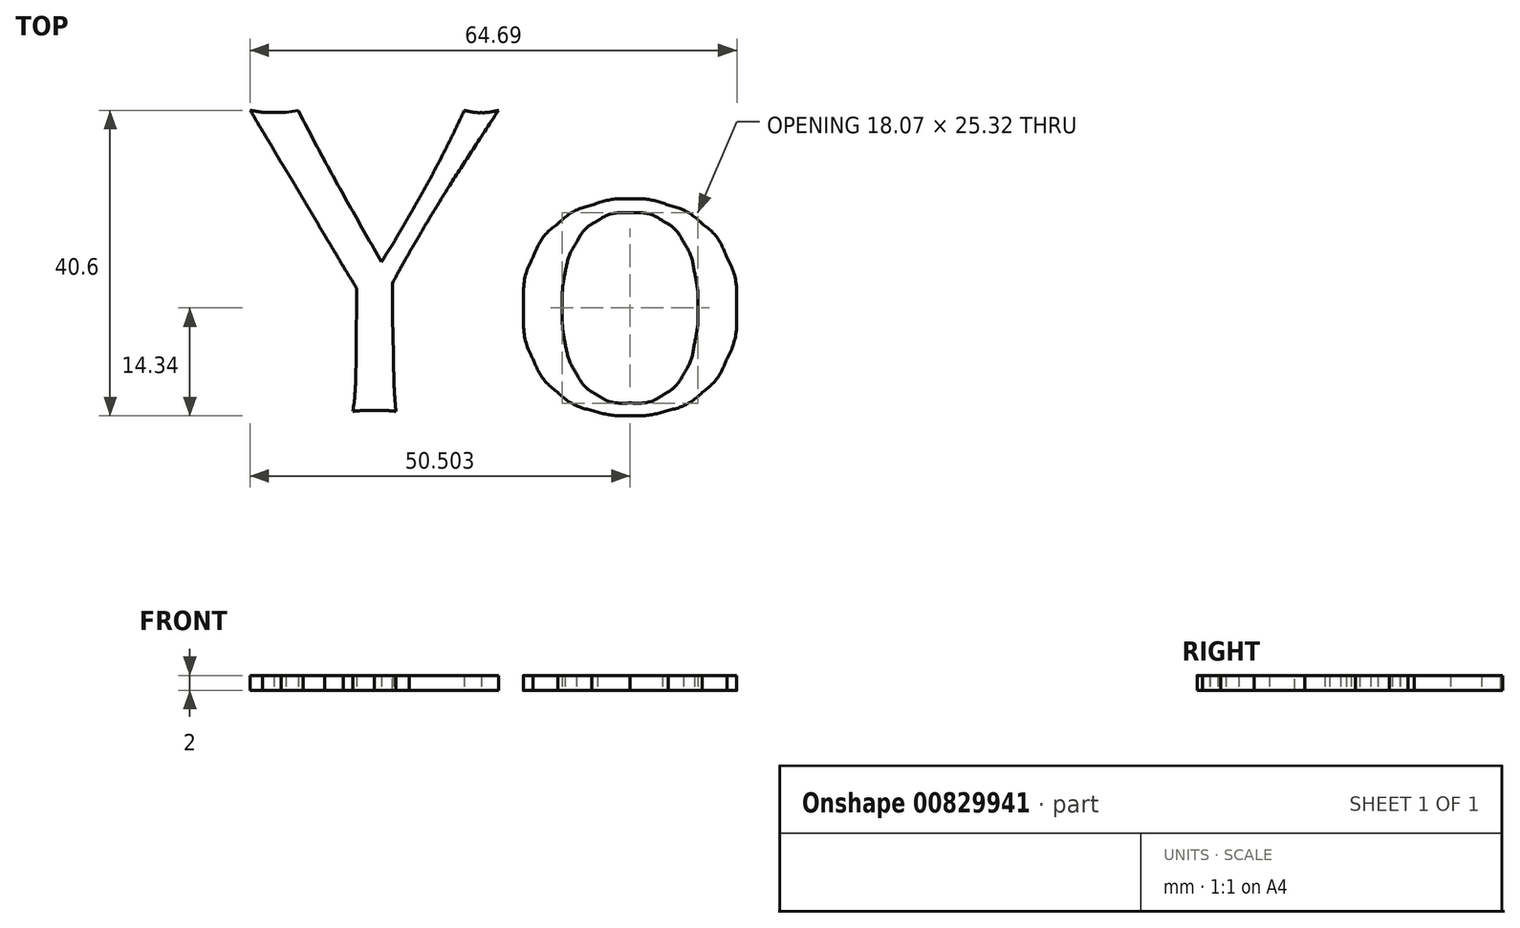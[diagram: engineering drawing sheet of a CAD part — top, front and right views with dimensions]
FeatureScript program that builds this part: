
annotation { "Feature Type Name" : "Feature", "Feature Type Description" : "" }
export const myFeature = defineFeature(function(context is Context, id is Id, definition is map)
    precondition{}
    {
        {
            var Q0;
            Q0=qCreatedBy(makeId("Top.planeOp"),FACE);
            var sketch = newSketch(context, id + "F0", { "sketchPlane" : qUnion([Q0])});
            skLineSegment(sketch, "E0", {"start": v(10.7, 31.08) * mm, "end": v(10.7, 30.96) * mm});
            skLineSegment(sketch, "E1", {"start": v(10.7, 30.96) * mm, "end": v(10.7, 31.08) * mm});
            skLineSegment(sketch, "E2", {"start": v(10.23, 21.47) * mm, "end": v(10.23, 21.36) * mm});
            skLineSegment(sketch, "E3", {"start": v(10.23, 21.36) * mm, "end": v(10.23, 21.47) * mm});
            skLineSegment(sketch, "E4", {"start": v(23.04, 46.92) * mm, "end": v(23.15, 47.03) * mm});
            skLineSegment(sketch, "E5", {"start": v(23.15, 47.03) * mm, "end": v(23.04, 46.92) * mm});
            skLineSegment(sketch, "E6", {"start": v(50.58, 35.45) * mm, "end": v(50.34, 26.71) * mm});
            skLineSegment(sketch, "E7", {"start": v(50.34, 26.71) * mm, "end": v(50.58, 35.45) * mm});
            skLineSegment(sketch, "E8", {"start": v(36.2, 45.81) * mm, "end": v(36.2, 42.78) * mm});
            skLineSegment(sketch, "E9", {"start": v(36.2, 42.78) * mm, "end": v(36.84, 42.78) * mm});
            skLineSegment(sketch, "E10", {"start": v(36.84, 42.78) * mm, "end": v(36.2, 45.81) * mm});
            skLineSegment(sketch, "E11", {"start": v(58.26, 21.65) * mm, "end": v(58.26, 22.93) * mm});
            skLineSegment(sketch, "E12", {"start": v(58.26, 22.93) * mm, "end": v(58.26, 21.65) * mm});
            skLineSegment(sketch, "E13", {"start": v(-22.09, -30.8) * mm, "end": v(-22.79, -30.8) * mm});
            skLineSegment(sketch, "E14", {"start": v(-22.79, -30.8) * mm, "end": v(-22.09, -30.8) * mm});
            skLineSegment(sketch, "E15", {"start": v(-9.57, -13.74) * mm, "end": v(-8.87, -13.74) * mm});
            skLineSegment(sketch, "E16", {"start": v(-8.87, -13.74) * mm, "end": v(-9.57, -13.74) * mm});
            skLineSegment(sketch, "E17", {"start": v(5.02, -26.08) * mm, "end": v(5.02, -26.2) * mm});
            skLineSegment(sketch, "E18", {"start": v(5.02, -26.2) * mm, "end": v(5.02, -26.08) * mm});
            skLineSegment(sketch, "E19", {"start": v(4.56, -35.7) * mm, "end": v(4.56, -35.8) * mm});
            skLineSegment(sketch, "E20", {"start": v(4.56, -35.8) * mm, "end": v(4.56, -35.7) * mm});
            skLineSegment(sketch, "E21", {"start": v(17.37, -10.25) * mm, "end": v(17.48, -10.13) * mm});
            skLineSegment(sketch, "E22", {"start": v(17.48, -10.13) * mm, "end": v(17.37, -10.25) * mm});
            skFitSpline(sketch, "E23", {"points": [v(-50.5, 37.3) * mm, v(-50.5, 34.17) * mm, v(-50.52, 31.16) * mm, v(-50.56, 28.29) * mm]});
            skFitSpline(sketch, "E24", {"points": [v(-50.56, 28.29) * mm, v(-50.6, 25.41) * mm, v(-50.73, 22.97) * mm, v(-50.96, 20.95) * mm]});
            skFitSpline(sketch, "E25", {"points": [v(-50.96, 20.95) * mm, v(-50.07, 21.03) * mm, v(-49.12, 21.07) * mm, v(-48.11, 21.07) * mm]});
            skFitSpline(sketch, "E26", {"points": [v(-48.11, 21.07) * mm, v(-47.1, 21.07) * mm, v(-46.15, 21.03) * mm, v(-45.26, 20.95) * mm]});
            skFitSpline(sketch, "E27", {"points": [v(-45.26, 20.95) * mm, v(-45.34, 21.76) * mm, v(-45.41, 22.83) * mm, v(-45.5, 24.15) * mm]});
            skFitSpline(sketch, "E28", {"points": [v(-45.5, 24.15) * mm, v(-45.53, 25.5) * mm, v(-45.57, 26.97) * mm, v(-45.6, 28.52) * mm]});
            skFitSpline(sketch, "E29", {"points": [v(-45.6, 28.52) * mm, v(-45.65, 30.1) * mm, v(-45.69, 31.72) * mm, v(-45.72, 33.35) * mm]});
            skFitSpline(sketch, "E30", {"points": [v(-45.72, 33.35) * mm, v(-45.72, 34.98) * mm, v(-45.72, 36.51) * mm, v(-45.72, 37.95) * mm]});
            skFitSpline(sketch, "E31", {"points": [v(-45.72, 37.95) * mm, v(-45.1, 39.15) * mm, v(-44.37, 40.5) * mm, v(-43.51, 41.97) * mm]});
            skFitSpline(sketch, "E32", {"points": [v(-43.51, 41.97) * mm, v(-42.66, 43.48) * mm, v(-41.67, 45.17) * mm, v(-40.54, 47.03) * mm]});
            skFitSpline(sketch, "E33", {"points": [v(-40.54, 47.03) * mm, v(-39.42, 48.9) * mm, v(-38.12, 50.97) * mm, v(-36.64, 53.26) * mm]});
            skFitSpline(sketch, "E34", {"points": [v(-36.64, 53.26) * mm, v(-35.17, 55.55) * mm, v(-33.5, 58.12) * mm, v(-31.63, 60.95) * mm]});
            skFitSpline(sketch, "E35", {"points": [v(-31.63, 60.95) * mm, v(-32.6, 60.75) * mm, v(-33.36, 60.66) * mm, v(-33.9, 60.66) * mm]});
            skFitSpline(sketch, "E36", {"points": [v(-33.9, 60.66) * mm, v(-34.45, 60.66) * mm, v(-35.2, 60.75) * mm, v(-36.18, 60.95) * mm]});
            skFitSpline(sketch, "E37", {"points": [v(-36.18, 60.95) * mm, v(-36.95, 59.28) * mm, v(-37.79, 57.55) * mm, v(-38.68, 55.77) * mm]});
            skFitSpline(sketch, "E38", {"points": [v(-38.68, 55.77) * mm, v(-39.57, 54.02) * mm, v(-40.5, 52.27) * mm, v(-41.47, 50.53) * mm]});
            skFitSpline(sketch, "E39", {"points": [v(-41.47, 50.53) * mm, v(-42.44, 48.78) * mm, v(-43.41, 47.07) * mm, v(-44.39, 45.4) * mm]});
            skFitSpline(sketch, "E40", {"points": [v(-44.39, 45.4) * mm, v(-45.36, 43.73) * mm, v(-46.29, 42.2) * mm, v(-47.18, 40.8) * mm]});
            skFitSpline(sketch, "E41", {"points": [v(-47.18, 40.8) * mm, v(-49.2, 44.34) * mm, v(-51.12, 47.73) * mm, v(-52.94, 51) * mm]});
            skFitSpline(sketch, "E42", {"points": [v(-52.94, 51) * mm, v(-54.73, 54.25) * mm, v(-56.5, 57.57) * mm, v(-58.24, 60.95) * mm]});
            skFitSpline(sketch, "E43", {"points": [v(-58.24, 60.95) * mm, v(-58.79, 60.87) * mm, v(-59.33, 60.8) * mm, v(-59.87, 60.72) * mm]});
            skFitSpline(sketch, "E44", {"points": [v(-59.87, 60.72) * mm, v(-60.38, 60.68) * mm, v(-60.9, 60.66) * mm, v(-61.44, 60.66) * mm]});
            skFitSpline(sketch, "E45", {"points": [v(-61.44, 60.66) * mm, v(-61.99, 60.66) * mm, v(-62.53, 60.68) * mm, v(-63.08, 60.72) * mm]});
            skFitSpline(sketch, "E46", {"points": [v(-63.08, 60.72) * mm, v(-63.58, 60.8) * mm, v(-64.1, 60.87) * mm, v(-64.65, 60.95) * mm]});
            skFitSpline(sketch, "E47", {"points": [v(-64.65, 60.95) * mm, v(-64.26, 60.33) * mm, v(-63.7, 59.4) * mm, v(-62.96, 58.15) * mm]});
            skFitSpline(sketch, "E48", {"points": [v(-62.96, 58.15) * mm, v(-62.22, 56.95) * mm, v(-61.4, 55.57) * mm, v(-60.51, 54.02) * mm]});
            skFitSpline(sketch, "E49", {"points": [v(-60.51, 54.02) * mm, v(-59.58, 52.5) * mm, v(-58.61, 50.9) * mm, v(-57.6, 49.19) * mm]});
            skFitSpline(sketch, "E50", {"points": [v(-57.6, 49.19) * mm, v(-56.6, 47.52) * mm, v(-55.64, 45.9) * mm, v(-54.75, 44.35) * mm]});
            skFitSpline(sketch, "E51", {"points": [v(-54.75, 44.35) * mm, v(-53.82, 42.84) * mm, v(-52.98, 41.44) * mm, v(-52.25, 40.16) * mm]});
            skFitSpline(sketch, "E52", {"points": [v(-52.25, 40.16) * mm, v(-51.47, 38.92) * mm, v(-50.89, 37.97) * mm, v(-50.5, 37.3) * mm]});
            skFitSpline(sketch, "E53", {"points": [v(-23.17, 34.69) * mm, v(-23.17, 36.32) * mm, v(-23.04, 37.9) * mm, v(-22.76, 39.4) * mm]});
            skFitSpline(sketch, "E54", {"points": [v(-22.76, 39.4) * mm, v(-22.45, 40.92) * mm, v(-21.95, 42.26) * mm, v(-21.25, 43.42) * mm]});
            skFitSpline(sketch, "E55", {"points": [v(-21.25, 43.42) * mm, v(-20.55, 44.63) * mm, v(-19.62, 45.58) * mm, v(-18.46, 46.28) * mm]});
            skFitSpline(sketch, "E56", {"points": [v(-18.46, 46.28) * mm, v(-17.3, 46.98) * mm, v(-15.86, 47.32) * mm, v(-14.15, 47.32) * mm]});
            skFitSpline(sketch, "E57", {"points": [v(-14.15, 47.32) * mm, v(-12.44, 47.32) * mm, v(-11, 46.98) * mm, v(-9.84, 46.28) * mm]});
            skFitSpline(sketch, "E58", {"points": [v(-9.84, 46.28) * mm, v(-8.67, 45.58) * mm, v(-7.74, 44.63) * mm, v(-7.04, 43.42) * mm]});
            skFitSpline(sketch, "E59", {"points": [v(-7.04, 43.42) * mm, v(-6.35, 42.26) * mm, v(-5.86, 40.92) * mm, v(-5.59, 39.4) * mm]});
            skFitSpline(sketch, "E60", {"points": [v(-5.59, 39.4) * mm, v(-5.28, 37.9) * mm, v(-5.12, 36.32) * mm, v(-5.12, 34.69) * mm]});
            skFitSpline(sketch, "E61", {"points": [v(-5.12, 34.69) * mm, v(-5.12, 33.06) * mm, v(-5.28, 31.49) * mm, v(-5.59, 29.97) * mm]});
            skFitSpline(sketch, "E62", {"points": [v(-5.59, 29.97) * mm, v(-5.86, 28.46) * mm, v(-6.35, 27.1) * mm, v(-7.04, 25.9) * mm]});
            skFitSpline(sketch, "E63", {"points": [v(-7.04, 25.9) * mm, v(-7.74, 24.73) * mm, v(-8.67, 23.8) * mm, v(-9.84, 23.1) * mm]});
            skFitSpline(sketch, "E64", {"points": [v(-9.84, 23.1) * mm, v(-11, 22.4) * mm, v(-12.44, 22.06) * mm, v(-14.15, 22.06) * mm]});
            skFitSpline(sketch, "E65", {"points": [v(-14.15, 22.06) * mm, v(-15.86, 22.06) * mm, v(-17.3, 22.4) * mm, v(-18.46, 23.1) * mm]});
            skFitSpline(sketch, "E66", {"points": [v(-18.46, 23.1) * mm, v(-19.62, 23.8) * mm, v(-20.55, 24.73) * mm, v(-21.25, 25.9) * mm]});
            skFitSpline(sketch, "E67", {"points": [v(-21.25, 25.9) * mm, v(-21.95, 27.1) * mm, v(-22.45, 28.46) * mm, v(-22.76, 29.97) * mm]});
            skFitSpline(sketch, "E68", {"points": [v(-22.76, 29.97) * mm, v(-23.04, 31.49) * mm, v(-23.17, 33.06) * mm, v(-23.17, 34.69) * mm]});
            skFitSpline(sketch, "E69", {"points": [v(-28.3, 34.69) * mm, v(-28.3, 32.05) * mm, v(-27.89, 29.8) * mm, v(-27.07, 27.94) * mm]});
            skFitSpline(sketch, "E70", {"points": [v(-27.07, 27.94) * mm, v(-26.22, 26.11) * mm, v(-25.11, 24.62) * mm, v(-23.75, 23.45) * mm]});
            skFitSpline(sketch, "E71", {"points": [v(-23.75, 23.45) * mm, v(-22.4, 22.33) * mm, v(-20.88, 21.53) * mm, v(-19.21, 21.07) * mm]});
            skFitSpline(sketch, "E72", {"points": [v(-19.21, 21.07) * mm, v(-17.5, 20.6) * mm, v(-15.82, 20.37) * mm, v(-14.15, 20.37) * mm]});
            skFitSpline(sketch, "E73", {"points": [v(-14.15, 20.37) * mm, v(-12.44, 20.37) * mm, v(-10.75, 20.6) * mm, v(-9.08, 21.07) * mm]});
            skFitSpline(sketch, "E74", {"points": [v(-9.08, 21.07) * mm, v(-7.41, 21.53) * mm, v(-5.9, 22.33) * mm, v(-4.54, 23.45) * mm]});
            skFitSpline(sketch, "E75", {"points": [v(-4.54, 23.45) * mm, v(-3.18, 24.62) * mm, v(-2.1, 26.11) * mm, v(-1.28, 27.94) * mm]});
            skFitSpline(sketch, "E76", {"points": [v(-1.28, 27.94) * mm, v(-0.43, 29.8) * mm, v(0, 32.05) * mm, v(0, 34.69) * mm]});
            skFitSpline(sketch, "E77", {"points": [v(0, 34.69) * mm, v(0, 37.33) * mm, v(-0.43, 39.56) * mm, v(-1.28, 41.39) * mm]});
            skFitSpline(sketch, "E78", {"points": [v(-1.28, 41.39) * mm, v(-2.1, 43.25) * mm, v(-3.18, 44.74) * mm, v(-4.54, 45.87) * mm]});
            skFitSpline(sketch, "E79", {"points": [v(-4.54, 45.87) * mm, v(-5.9, 47.03) * mm, v(-7.41, 47.87) * mm, v(-9.08, 48.37) * mm]});
            skFitSpline(sketch, "E80", {"points": [v(-9.08, 48.37) * mm, v(-10.75, 48.92) * mm, v(-12.44, 49.19) * mm, v(-14.15, 49.19) * mm]});
            skFitSpline(sketch, "E81", {"points": [v(-14.15, 49.19) * mm, v(-15.82, 49.19) * mm, v(-17.5, 48.92) * mm, v(-19.21, 48.37) * mm]});
            skFitSpline(sketch, "E82", {"points": [v(-19.21, 48.37) * mm, v(-20.88, 47.87) * mm, v(-22.4, 47.03) * mm, v(-23.75, 45.87) * mm]});
            skFitSpline(sketch, "E83", {"points": [v(-23.75, 45.87) * mm, v(-25.11, 44.74) * mm, v(-26.22, 43.25) * mm, v(-27.07, 41.39) * mm]});
            skFitSpline(sketch, "E84", {"points": [v(-27.07, 41.39) * mm, v(-27.89, 39.56) * mm, v(-28.3, 37.33) * mm, v(-28.3, 34.69) * mm]});
            skFitSpline(sketch, "E85", {"points": [v(25.66, 14.78) * mm, v(25.66, 13.46) * mm, v(25.39, 12.33) * mm, v(24.84, 11.4) * mm]});
            skFitSpline(sketch, "E86", {"points": [v(24.84, 11.4) * mm, v(24.3, 10.43) * mm, v(23.58, 9.63) * mm, v(22.69, 9.01) * mm]});
            skFitSpline(sketch, "E87", {"points": [v(22.69, 9.01) * mm, v(21.83, 8.4) * mm, v(20.84, 7.93) * mm, v(19.72, 7.62) * mm]});
            skFitSpline(sketch, "E88", {"points": [v(19.72, 7.62) * mm, v(18.6, 7.3) * mm, v(17.45, 7.15) * mm, v(16.28, 7.15) * mm]});
            skFitSpline(sketch, "E89", {"points": [v(16.28, 7.15) * mm, v(15.08, 7.15) * mm, v(13.95, 7.29) * mm, v(12.9, 7.56) * mm]});
            skFitSpline(sketch, "E90", {"points": [v(12.9, 7.56) * mm, v(11.86, 7.83) * mm, v(10.95, 8.26) * mm, v(10.17, 8.84) * mm]});
            skFitSpline(sketch, "E91", {"points": [v(10.17, 8.84) * mm, v(9.43, 9.42) * mm, v(8.83, 10.18) * mm, v(8.36, 11.1) * mm]});
            skFitSpline(sketch, "E92", {"points": [v(8.36, 11.1) * mm, v(7.94, 12.04) * mm, v(7.72, 13.17) * mm, v(7.72, 14.49) * mm]});
            skFitSpline(sketch, "E93", {"points": [v(7.72, 14.49) * mm, v(7.72, 16.97) * mm, v(8.52, 18.7) * mm, v(10.11, 19.67) * mm]});
            skFitSpline(sketch, "E94", {"points": [v(10.11, 19.67) * mm, v(11.7, 20.6) * mm, v(13.95, 21.07) * mm, v(16.86, 21.07) * mm]});
            skFitSpline(sketch, "E95", {"points": [v(16.86, 21.07) * mm, v(20, 21.07) * mm, v(22.26, 20.6) * mm, v(23.62, 19.67) * mm]});
            skFitSpline(sketch, "E96", {"points": [v(23.62, 19.67) * mm, v(24.98, 18.74) * mm, v(25.66, 17.1) * mm, v(25.66, 14.78) * mm]});
            skFitSpline(sketch, "E97", {"points": [v(22.51, 39.99) * mm, v(22.51, 38.9) * mm, v(22.38, 37.85) * mm, v(22.1, 36.84) * mm]});
            skFitSpline(sketch, "E98", {"points": [v(22.1, 36.84) * mm, v(21.87, 35.87) * mm, v(21.48, 35) * mm, v(20.94, 34.22) * mm]});
            skFitSpline(sketch, "E99", {"points": [v(20.94, 34.22) * mm, v(20.44, 33.49) * mm, v(19.78, 32.88) * mm, v(18.96, 32.42) * mm]});
            skFitSpline(sketch, "E100", {"points": [v(18.96, 32.42) * mm, v(18.18, 32) * mm, v(17.23, 31.78) * mm, v(16.1, 31.78) * mm]});
            skFitSpline(sketch, "E101", {"points": [v(16.1, 31.78) * mm, v(13.86, 31.78) * mm, v(12.19, 32.48) * mm, v(11.1, 33.87) * mm]});
            skFitSpline(sketch, "E102", {"points": [v(11.1, 33.87) * mm, v(10.05, 35.31) * mm, v(9.53, 37.25) * mm, v(9.53, 39.7) * mm]});
            skFitSpline(sketch, "E103", {"points": [v(9.53, 39.7) * mm, v(9.53, 42.06) * mm, v(10.11, 43.95) * mm, v(11.28, 45.34) * mm]});
            skFitSpline(sketch, "E104", {"points": [v(11.28, 45.34) * mm, v(12.44, 46.78) * mm, v(14.07, 47.5) * mm, v(16.17, 47.5) * mm]});
            skFitSpline(sketch, "E105", {"points": [v(16.17, 47.5) * mm, v(18.07, 47.5) * mm, v(19.6, 46.86) * mm, v(20.77, 45.58) * mm]});
            skFitSpline(sketch, "E106", {"points": [v(20.77, 45.58) * mm, v(21.93, 44.3) * mm, v(22.51, 42.43) * mm, v(22.51, 39.99) * mm]});
            skFitSpline(sketch, "E107", {"points": [v(4.99, 39.7) * mm, v(4.99, 37.56) * mm, v(5.5, 35.78) * mm, v(6.5, 34.34) * mm]});
            skFitSpline(sketch, "E108", {"points": [v(6.5, 34.34) * mm, v(7.51, 32.94) * mm, v(8.9, 31.86) * mm, v(10.7, 31.08) * mm]});
            skFitSpline(sketch, "E109", {"points": [v(10.7, 30.96) * mm, v(10.23, 30.89) * mm, v(9.74, 30.71) * mm, v(9.24, 30.44) * mm]});
            skFitSpline(sketch, "E110", {"points": [v(9.24, 30.44) * mm, v(8.73, 30.17) * mm, v(8.29, 29.82) * mm, v(7.9, 29.4) * mm]});
            skFitSpline(sketch, "E111", {"points": [v(7.9, 29.4) * mm, v(7.51, 28.96) * mm, v(7.18, 28.48) * mm, v(6.9, 27.94) * mm]});
            skFitSpline(sketch, "E112", {"points": [v(6.9, 27.94) * mm, v(6.68, 27.4) * mm, v(6.56, 26.8) * mm, v(6.56, 26.13) * mm]});
            skFitSpline(sketch, "E113", {"points": [v(6.56, 26.13) * mm, v(6.56, 25) * mm, v(6.87, 24.03) * mm, v(7.5, 23.22) * mm]});
            skFitSpline(sketch, "E114", {"points": [v(7.5, 23.22) * mm, v(8.11, 22.4) * mm, v(9.02, 21.82) * mm, v(10.23, 21.47) * mm]});
            skFitSpline(sketch, "E115", {"points": [v(10.23, 21.36) * mm, v(9.45, 21.16) * mm, v(8.7, 20.87) * mm, v(7.96, 20.48) * mm]});
            skFitSpline(sketch, "E116", {"points": [v(7.96, 20.48) * mm, v(7.22, 20.1) * mm, v(6.56, 19.57) * mm, v(5.98, 18.91) * mm]});
            skFitSpline(sketch, "E117", {"points": [v(5.98, 18.91) * mm, v(5.4, 18.25) * mm, v(4.9, 17.5) * mm, v(4.52, 16.64) * mm]});
            skFitSpline(sketch, "E118", {"points": [v(4.52, 16.64) * mm, v(4.17, 15.79) * mm, v(4, 14.85) * mm, v(4, 13.85) * mm]});
            skFitSpline(sketch, "E119", {"points": [v(4, 13.85) * mm, v(4, 11.24) * mm, v(5.08, 9.2) * mm, v(7.26, 7.73) * mm]});
            skFitSpline(sketch, "E120", {"points": [v(7.26, 7.73) * mm, v(9.43, 6.22) * mm, v(12.4, 5.46) * mm, v(16.17, 5.46) * mm]});
            skFitSpline(sketch, "E121", {"points": [v(16.17, 5.46) * mm, v(18.61, 5.46) * mm, v(20.7, 5.83) * mm, v(22.45, 6.57) * mm]});
            skFitSpline(sketch, "E122", {"points": [v(22.45, 6.57) * mm, v(24.2, 7.3) * mm, v(25.62, 8.24) * mm, v(26.7, 9.36) * mm]});
            skFitSpline(sketch, "E123", {"points": [v(26.7, 9.36) * mm, v(27.83, 10.49) * mm, v(28.65, 11.75) * mm, v(29.15, 13.15) * mm]});
            skFitSpline(sketch, "E124", {"points": [v(29.15, 13.15) * mm, v(29.7, 14.54) * mm, v(29.97, 15.92) * mm, v(29.97, 17.28) * mm]});
            skFitSpline(sketch, "E125", {"points": [v(29.97, 17.28) * mm, v(29.97, 18.29) * mm, v(29.77, 19.22) * mm, v(29.38, 20.08) * mm]});
            skFitSpline(sketch, "E126", {"points": [v(29.38, 20.08) * mm, v(29.03, 20.93) * mm, v(28.45, 21.69) * mm, v(27.64, 22.35) * mm]});
            skFitSpline(sketch, "E127", {"points": [v(27.64, 22.35) * mm, v(26.86, 23) * mm, v(25.83, 23.53) * mm, v(24.55, 23.92) * mm]});
            skFitSpline(sketch, "E128", {"points": [v(24.55, 23.92) * mm, v(23.3, 24.3) * mm, v(21.8, 24.52) * mm, v(20, 24.56) * mm]});
            skFitSpline(sketch, "E129", {"points": [v(20, 24.56) * mm, v(18.92, 24.6) * mm, v(17.85, 24.62) * mm, v(16.8, 24.62) * mm]});
            skFitSpline(sketch, "E130", {"points": [v(16.8, 24.62) * mm, v(15.76, 24.66) * mm, v(14.7, 24.7) * mm, v(13.6, 24.73) * mm]});
            skFitSpline(sketch, "E131", {"points": [v(13.6, 24.73) * mm, v(12.28, 24.77) * mm, v(11.37, 25.02) * mm, v(10.87, 25.5) * mm]});
            skFitSpline(sketch, "E132", {"points": [v(10.87, 25.5) * mm, v(10.4, 25.96) * mm, v(10.17, 26.7) * mm, v(10.17, 27.7) * mm]});
            skFitSpline(sketch, "E133", {"points": [v(10.17, 27.7) * mm, v(10.17, 28.48) * mm, v(10.46, 29.12) * mm, v(11.04, 29.62) * mm]});
            skFitSpline(sketch, "E134", {"points": [v(11.04, 29.62) * mm, v(11.66, 30.13) * mm, v(12.32, 30.38) * mm, v(13.02, 30.38) * mm]});
            skFitSpline(sketch, "E135", {"points": [v(13.02, 30.38) * mm, v(13.57, 30.38) * mm, v(14.09, 30.36) * mm, v(14.6, 30.32) * mm]});
            skFitSpline(sketch, "E136", {"points": [v(14.6, 30.32) * mm, v(15.14, 30.28) * mm, v(15.68, 30.26) * mm, v(16.22, 30.26) * mm]});
            skFitSpline(sketch, "E137", {"points": [v(16.22, 30.26) * mm, v(19.52, 30.26) * mm, v(22.14, 31.08) * mm, v(24.08, 32.71) * mm]});
            skFitSpline(sketch, "E138", {"points": [v(24.08, 32.71) * mm, v(26.06, 34.38) * mm, v(27.05, 36.67) * mm, v(27.05, 39.58) * mm]});
            skFitSpline(sketch, "E139", {"points": [v(27.05, 39.58) * mm, v(27.05, 41.06) * mm, v(26.69, 42.47) * mm, v(25.95, 43.83) * mm]});
            skFitSpline(sketch, "E140", {"points": [v(25.95, 43.83) * mm, v(25.21, 45.23) * mm, v(24.24, 46.26) * mm, v(23.04, 46.92) * mm]});
            skFitSpline(sketch, "E141", {"points": [v(23.15, 47.03) * mm, v(24.2, 47) * mm, v(25.25, 46.92) * mm, v(26.3, 46.8) * mm]});
            skFitSpline(sketch, "E142", {"points": [v(26.3, 46.8) * mm, v(27.38, 46.72) * mm, v(28.5, 46.65) * mm, v(29.62, 46.57) * mm]});
            skFitSpline(sketch, "E143", {"points": [v(29.62, 46.57) * mm, v(29.58, 46.76) * mm, v(29.54, 46.96) * mm, v(29.5, 47.15) * mm]});
            skFitSpline(sketch, "E144", {"points": [v(29.5, 47.15) * mm, v(29.5, 47.38) * mm, v(29.5, 47.6) * mm, v(29.5, 47.8) * mm]});
            skFitSpline(sketch, "E145", {"points": [v(29.5, 47.8) * mm, v(29.5, 47.98) * mm, v(29.5, 48.18) * mm, v(29.5, 48.37) * mm]});
            skFitSpline(sketch, "E146", {"points": [v(29.5, 48.37) * mm, v(29.54, 48.6) * mm, v(29.58, 48.82) * mm, v(29.62, 49.01) * mm]});
            skFitSpline(sketch, "E147", {"points": [v(29.62, 49.01) * mm, v(28.65, 48.82) * mm, v(27.07, 48.72) * mm, v(24.9, 48.72) * mm]});
            skFitSpline(sketch, "E148", {"points": [v(24.9, 48.72) * mm, v(24.47, 48.72) * mm, v(23.91, 48.74) * mm, v(23.21, 48.78) * mm]});
            skFitSpline(sketch, "E149", {"points": [v(23.21, 48.78) * mm, v(22.51, 48.82) * mm, v(21.72, 48.88) * mm, v(20.82, 48.95) * mm]});
            skFitSpline(sketch, "E150", {"points": [v(20.82, 48.95) * mm, v(19.78, 49.03) * mm, v(18.9, 49.1) * mm, v(18.2, 49.13) * mm]});
            skFitSpline(sketch, "E151", {"points": [v(18.2, 49.13) * mm, v(17.54, 49.17) * mm, v(16.85, 49.19) * mm, v(16.1, 49.19) * mm]});
            skFitSpline(sketch, "E152", {"points": [v(16.1, 49.19) * mm, v(14.6, 49.19) * mm, v(13.16, 49) * mm, v(11.8, 48.6) * mm]});
            skFitSpline(sketch, "E153", {"points": [v(11.8, 48.6) * mm, v(10.48, 48.22) * mm, v(9.3, 47.63) * mm, v(8.25, 46.86) * mm]});
            skFitSpline(sketch, "E154", {"points": [v(8.25, 46.86) * mm, v(7.24, 46.08) * mm, v(6.44, 45.1) * mm, v(5.86, 43.89) * mm]});
            skFitSpline(sketch, "E155", {"points": [v(5.86, 43.89) * mm, v(5.28, 42.72) * mm, v(4.99, 41.33) * mm, v(4.99, 39.7) * mm]});
            skFitSpline(sketch, "E156", {"points": [v(50.34, 26.71) * mm, v(49.68, 25.63) * mm, v(48.73, 24.68) * mm, v(47.5, 23.86) * mm]});
            skFitSpline(sketch, "E157", {"points": [v(47.5, 23.86) * mm, v(46.29, 23.04) * mm, v(44.95, 22.64) * mm, v(43.47, 22.64) * mm]});
            skFitSpline(sketch, "E158", {"points": [v(43.47, 22.64) * mm, v(42.2, 22.64) * mm, v(41.03, 23.1) * mm, v(39.98, 24.03) * mm]});
            skFitSpline(sketch, "E159", {"points": [v(39.98, 24.03) * mm, v(38.93, 24.97) * mm, v(38.4, 26.34) * mm, v(38.4, 28.17) * mm]});
            skFitSpline(sketch, "E160", {"points": [v(38.4, 28.17) * mm, v(38.4, 29.26) * mm, v(38.6, 30.15) * mm, v(39, 30.85) * mm]});
            skFitSpline(sketch, "E161", {"points": [v(39, 30.85) * mm, v(39.42, 31.55) * mm, v(39.96, 32.13) * mm, v(40.62, 32.6) * mm]});
            skFitSpline(sketch, "E162", {"points": [v(40.62, 32.6) * mm, v(41.32, 33.06) * mm, v(42.1, 33.43) * mm, v(42.95, 33.7) * mm]});
            skFitSpline(sketch, "E163", {"points": [v(42.95, 33.7) * mm, v(43.84, 33.97) * mm, v(44.73, 34.19) * mm, v(45.63, 34.34) * mm]});
            skFitSpline(sketch, "E164", {"points": [v(45.63, 34.34) * mm, v(46.52, 34.53) * mm, v(47.4, 34.7) * mm, v(48.25, 34.86) * mm]});
            skFitSpline(sketch, "E165", {"points": [v(48.25, 34.86) * mm, v(49.14, 35.02) * mm, v(49.92, 35.21) * mm, v(50.58, 35.45) * mm]});
            skFitSpline(sketch, "E166", {"points": [v(36.84, 42.78) * mm, v(37.5, 44.02) * mm, v(38.49, 45) * mm, v(39.8, 45.7) * mm]});
            skFitSpline(sketch, "E167", {"points": [v(39.8, 45.7) * mm, v(41.16, 46.4) * mm, v(42.62, 46.74) * mm, v(44.17, 46.74) * mm]});
            skFitSpline(sketch, "E168", {"points": [v(44.17, 46.74) * mm, v(45.34, 46.74) * mm, v(46.33, 46.53) * mm, v(47.14, 46.1) * mm]});
            skFitSpline(sketch, "E169", {"points": [v(47.14, 46.1) * mm, v(47.96, 45.71) * mm, v(48.62, 45.19) * mm, v(49.12, 44.53) * mm]});
            skFitSpline(sketch, "E170", {"points": [v(49.12, 44.53) * mm, v(49.63, 43.87) * mm, v(50, 43.1) * mm, v(50.23, 42.2) * mm]});
            skFitSpline(sketch, "E171", {"points": [v(50.23, 42.2) * mm, v(50.46, 41.3) * mm, v(50.58, 40.38) * mm, v(50.58, 39.4) * mm]});
            skFitSpline(sketch, "E172", {"points": [v(50.58, 39.4) * mm, v(50.58, 38.82) * mm, v(50.52, 38.34) * mm, v(50.4, 37.95) * mm]});
            skFitSpline(sketch, "E173", {"points": [v(50.4, 37.95) * mm, v(50.29, 37.6) * mm, v(49.94, 37.3) * mm, v(49.35, 37.02) * mm]});
            skFitSpline(sketch, "E174", {"points": [v(49.35, 37.02) * mm, v(48.81, 36.75) * mm, v(47.94, 36.48) * mm, v(46.73, 36.2) * mm]});
            skFitSpline(sketch, "E175", {"points": [v(46.73, 36.2) * mm, v(45.57, 35.97) * mm, v(43.94, 35.68) * mm, v(41.84, 35.33) * mm]});
            skFitSpline(sketch, "E176", {"points": [v(41.84, 35.33) * mm, v(39.28, 34.9) * mm, v(37.26, 34.05) * mm, v(35.79, 32.77) * mm]});
            skFitSpline(sketch, "E177", {"points": [v(35.79, 32.77) * mm, v(34.35, 31.49) * mm, v(33.63, 29.68) * mm, v(33.63, 27.35) * mm]});
            skFitSpline(sketch, "E178", {"points": [v(33.63, 27.35) * mm, v(33.63, 26.23) * mm, v(33.85, 25.22) * mm, v(34.27, 24.33) * mm]});
            skFitSpline(sketch, "E179", {"points": [v(34.27, 24.33) * mm, v(34.74, 23.47) * mm, v(35.32, 22.73) * mm, v(36.02, 22.11) * mm]});
            skFitSpline(sketch, "E180", {"points": [v(36.02, 22.11) * mm, v(36.76, 21.5) * mm, v(37.6, 21.05) * mm, v(38.52, 20.77) * mm]});
            skFitSpline(sketch, "E181", {"points": [v(38.52, 20.77) * mm, v(39.46, 20.5) * mm, v(40.4, 20.37) * mm, v(41.38, 20.37) * mm]});
            skFitSpline(sketch, "E182", {"points": [v(41.38, 20.37) * mm, v(43.36, 20.37) * mm, v(45.03, 20.7) * mm, v(46.38, 21.36) * mm]});
            skFitSpline(sketch, "E183", {"points": [v(46.38, 21.36) * mm, v(47.74, 22.02) * mm, v(49.12, 23.04) * mm, v(50.52, 24.44) * mm]});
            skFitSpline(sketch, "E184", {"points": [v(50.52, 24.44) * mm, v(50.63, 23.43) * mm, v(51.02, 22.6) * mm, v(51.68, 21.94) * mm]});
            skFitSpline(sketch, "E185", {"points": [v(51.68, 21.94) * mm, v(52.34, 21.32) * mm, v(53.3, 21) * mm, v(54.54, 21) * mm]});
            skFitSpline(sketch, "E186", {"points": [v(54.54, 21) * mm, v(55.31, 21) * mm, v(56.01, 21.07) * mm, v(56.63, 21.18) * mm]});
            skFitSpline(sketch, "E187", {"points": [v(56.63, 21.18) * mm, v(57.3, 21.3) * mm, v(57.84, 21.45) * mm, v(58.26, 21.65) * mm]});
            skFitSpline(sketch, "E188", {"points": [v(58.26, 22.93) * mm, v(58.07, 22.81) * mm, v(57.85, 22.73) * mm, v(57.62, 22.7) * mm]});
            skFitSpline(sketch, "E189", {"points": [v(57.62, 22.7) * mm, v(57.43, 22.7) * mm, v(57.23, 22.7) * mm, v(57.04, 22.7) * mm]});
            skFitSpline(sketch, "E190", {"points": [v(57.04, 22.7) * mm, v(56.46, 22.7) * mm, v(56.01, 22.83) * mm, v(55.7, 23.1) * mm]});
            skFitSpline(sketch, "E191", {"points": [v(55.7, 23.1) * mm, v(55.43, 23.37) * mm, v(55.22, 23.7) * mm, v(55.06, 24.1) * mm]});
            skFitSpline(sketch, "E192", {"points": [v(55.06, 24.1) * mm, v(54.9, 24.52) * mm, v(54.8, 24.99) * mm, v(54.77, 25.5) * mm]});
            skFitSpline(sketch, "E193", {"points": [v(54.77, 25.5) * mm, v(54.77, 26.03) * mm, v(54.77, 26.54) * mm, v(54.77, 27) * mm]});
            skFitSpline(sketch, "E194", {"points": [v(54.77, 27) * mm, v(54.77, 29.45) * mm, v(54.8, 31.76) * mm, v(54.89, 33.93) * mm]});
            skFitSpline(sketch, "E195", {"points": [v(54.89, 33.93) * mm, v(54.96, 36.15) * mm, v(55, 38.36) * mm, v(55, 40.57) * mm]});
            skFitSpline(sketch, "E196", {"points": [v(55, 40.57) * mm, v(55, 41.85) * mm, v(54.77, 43.02) * mm, v(54.3, 44.06) * mm]});
            skFitSpline(sketch, "E197", {"points": [v(54.3, 44.06) * mm, v(53.84, 45.15) * mm, v(53.2, 46.06) * mm, v(52.38, 46.8) * mm]});
            skFitSpline(sketch, "E198", {"points": [v(52.38, 46.8) * mm, v(51.57, 47.58) * mm, v(50.58, 48.16) * mm, v(49.41, 48.55) * mm]});
            skFitSpline(sketch, "E199", {"points": [v(49.41, 48.55) * mm, v(48.25, 48.97) * mm, v(46.97, 49.19) * mm, v(45.57, 49.19) * mm]});
            skFitSpline(sketch, "E200", {"points": [v(45.57, 49.19) * mm, v(44.02, 49.19) * mm, v(42.5, 48.95) * mm, v(41.03, 48.49) * mm]});
            skFitSpline(sketch, "E201", {"points": [v(41.03, 48.49) * mm, v(39.55, 48.02) * mm, v(37.94, 47.13) * mm, v(36.2, 45.81) * mm]});
            skFitSpline(sketch, "E202", {"points": [v(-22.79, -30.8) * mm, v(-22.79, -31.38) * mm, v(-22.92, -32.12) * mm, v(-23.2, -33.01) * mm]});
            skFitSpline(sketch, "E203", {"points": [v(-23.2, -33.01) * mm, v(-23.43, -33.87) * mm, v(-23.66, -34.55) * mm, v(-23.9, -35.05) * mm]});
            skFitSpline(sketch, "E204", {"points": [v(-23.9, -35.05) * mm, v(-23.08, -35.52) * mm, v(-22.07, -35.92) * mm, v(-20.87, -36.27) * mm]});
            skFitSpline(sketch, "E205", {"points": [v(-20.87, -36.27) * mm, v(-19.66, -36.62) * mm, v(-18.17, -36.8) * mm, v(-16.38, -36.8) * mm]});
            skFitSpline(sketch, "E206", {"points": [v(-16.38, -36.8) * mm, v(-14.75, -36.8) * mm, v(-13.3, -36.56) * mm, v(-12.02, -36.1) * mm]});
            skFitSpline(sketch, "E207", {"points": [v(-12.02, -36.1) * mm, v(-10.74, -35.6) * mm, v(-9.65, -34.91) * mm, v(-8.76, -34.06) * mm]});
            skFitSpline(sketch, "E208", {"points": [v(-8.76, -34.06) * mm, v(-7.82, -33.17) * mm, v(-7.13, -32.18) * mm, v(-6.66, -31.1) * mm]});
            skFitSpline(sketch, "E209", {"points": [v(-6.66, -31.1) * mm, v(-6.15, -30) * mm, v(-5.9, -28.9) * mm, v(-5.9, -27.77) * mm]});
            skFitSpline(sketch, "E210", {"points": [v(-5.9, -27.77) * mm, v(-5.9, -26.14) * mm, v(-6.25, -24.86) * mm, v(-6.95, -23.93) * mm]});
            skFitSpline(sketch, "E211", {"points": [v(-6.95, -23.93) * mm, v(-7.61, -23) * mm, v(-8.44, -22.28) * mm, v(-9.45, -21.77) * mm]});
            skFitSpline(sketch, "E212", {"points": [v(-9.45, -21.77) * mm, v(-10.46, -21.23) * mm, v(-11.57, -20.82) * mm, v(-12.77, -20.55) * mm]});
            skFitSpline(sketch, "E213", {"points": [v(-12.77, -20.55) * mm, v(-13.98, -20.24) * mm, v(-15.08, -19.9) * mm, v(-16.1, -19.5) * mm]});
            skFitSpline(sketch, "E214", {"points": [v(-16.1, -19.5) * mm, v(-17.1, -19.12) * mm, v(-17.95, -18.6) * mm, v(-18.65, -17.93) * mm]});
            skFitSpline(sketch, "E215", {"points": [v(-18.65, -17.93) * mm, v(-19.31, -17.23) * mm, v(-19.64, -16.26) * mm, v(-19.64, -15.02) * mm]});
            skFitSpline(sketch, "E216", {"points": [v(-19.64, -15.02) * mm, v(-19.64, -14.17) * mm, v(-19.49, -13.43) * mm, v(-19.18, -12.8) * mm]});
            skFitSpline(sketch, "E217", {"points": [v(-19.18, -12.8) * mm, v(-18.87, -12.19) * mm, v(-18.48, -11.68) * mm, v(-18.01, -11.3) * mm]});
            skFitSpline(sketch, "E218", {"points": [v(-18.01, -11.3) * mm, v(-17.55, -10.9) * mm, v(-17.02, -10.62) * mm, v(-16.44, -10.42) * mm]});
            skFitSpline(sketch, "E219", {"points": [v(-16.44, -10.42) * mm, v(-15.86, -10.23) * mm, v(-15.28, -10.13) * mm, v(-14.7, -10.13) * mm]});
            skFitSpline(sketch, "E220", {"points": [v(-14.7, -10.13) * mm, v(-13.37, -10.13) * mm, v(-12.27, -10.5) * mm, v(-11.38, -11.24) * mm]});
            skFitSpline(sketch, "E221", {"points": [v(-11.38, -11.24) * mm, v(-10.48, -11.97) * mm, v(-9.88, -12.8) * mm, v(-9.57, -13.74) * mm]});
            skFitSpline(sketch, "E222", {"points": [v(-8.87, -13.74) * mm, v(-8.8, -13.27) * mm, v(-8.62, -12.61) * mm, v(-8.35, -11.76) * mm]});
            skFitSpline(sketch, "E223", {"points": [v(-8.35, -11.76) * mm, v(-8.08, -10.9) * mm, v(-7.79, -10.19) * mm, v(-7.47, -9.6) * mm]});
            skFitSpline(sketch, "E224", {"points": [v(-7.47, -9.6) * mm, v(-8.37, -9.3) * mm, v(-9.32, -8.95) * mm, v(-10.33, -8.56) * mm]});
            skFitSpline(sketch, "E225", {"points": [v(-10.33, -8.56) * mm, v(-11.3, -8.17) * mm, v(-12.5, -7.98) * mm, v(-13.94, -7.98) * mm]});
            skFitSpline(sketch, "E226", {"points": [v(-13.94, -7.98) * mm, v(-15.5, -7.98) * mm, v(-16.87, -8.2) * mm, v(-18.07, -8.67) * mm]});
            skFitSpline(sketch, "E227", {"points": [v(-18.07, -8.67) * mm, v(-19.27, -9.1) * mm, v(-20.28, -9.7) * mm, v(-21.1, -10.48) * mm]});
            skFitSpline(sketch, "E228", {"points": [v(-21.1, -10.48) * mm, v(-21.91, -11.26) * mm, v(-22.54, -12.19) * mm, v(-22.96, -13.27) * mm]});
            skFitSpline(sketch, "E229", {"points": [v(-22.96, -13.27) * mm, v(-23.39, -14.32) * mm, v(-23.6, -15.49) * mm, v(-23.6, -16.77) * mm]});
            skFitSpline(sketch, "E230", {"points": [v(-23.6, -16.77) * mm, v(-23.6, -18.4) * mm, v(-23.27, -19.68) * mm, v(-22.61, -20.61) * mm]});
            skFitSpline(sketch, "E231", {"points": [v(-22.61, -20.61) * mm, v(-21.91, -21.54) * mm, v(-21.06, -22.3) * mm, v(-20.05, -22.88) * mm]});
            skFitSpline(sketch, "E232", {"points": [v(-20.05, -22.88) * mm, v(-19.04, -23.42) * mm, v(-17.94, -23.85) * mm, v(-16.73, -24.16) * mm]});
            skFitSpline(sketch, "E233", {"points": [v(-16.73, -24.16) * mm, v(-15.53, -24.47) * mm, v(-14.42, -24.84) * mm, v(-13.41, -25.27) * mm]});
            skFitSpline(sketch, "E234", {"points": [v(-13.41, -25.27) * mm, v(-12.4, -25.66) * mm, v(-11.57, -26.18) * mm, v(-10.9, -26.84) * mm]});
            skFitSpline(sketch, "E235", {"points": [v(-10.9, -26.84) * mm, v(-10.21, -27.46) * mm, v(-9.86, -28.37) * mm, v(-9.86, -29.58) * mm]});
            skFitSpline(sketch, "E236", {"points": [v(-9.86, -29.58) * mm, v(-9.86, -30.43) * mm, v(-10.02, -31.19) * mm, v(-10.33, -31.85) * mm]});
            skFitSpline(sketch, "E237", {"points": [v(-10.33, -31.85) * mm, v(-10.64, -32.5) * mm, v(-11.07, -33.05) * mm, v(-11.6, -33.48) * mm]});
            skFitSpline(sketch, "E238", {"points": [v(-11.6, -33.48) * mm, v(-12.11, -33.9) * mm, v(-12.71, -34.23) * mm, v(-13.41, -34.47) * mm]});
            skFitSpline(sketch, "E239", {"points": [v(-13.41, -34.47) * mm, v(-14.07, -34.7) * mm, v(-14.77, -34.82) * mm, v(-15.5, -34.82) * mm]});
            skFitSpline(sketch, "E240", {"points": [v(-15.5, -34.82) * mm, v(-16.32, -34.82) * mm, v(-17.1, -34.68) * mm, v(-17.84, -34.4) * mm]});
            skFitSpline(sketch, "E241", {"points": [v(-17.84, -34.4) * mm, v(-18.54, -34.14) * mm, v(-19.18, -33.8) * mm, v(-19.76, -33.42) * mm]});
            skFitSpline(sketch, "E242", {"points": [v(-19.76, -33.42) * mm, v(-20.3, -33) * mm, v(-20.79, -32.55) * mm, v(-21.22, -32.08) * mm]});
            skFitSpline(sketch, "E243", {"points": [v(-21.22, -32.08) * mm, v(-21.6, -31.61) * mm, v(-21.9, -31.19) * mm, v(-22.09, -30.8) * mm]});
            skFitSpline(sketch, "E244", {"points": [v(19.99, -42.39) * mm, v(19.99, -43.7) * mm, v(19.72, -44.83) * mm, v(19.17, -45.76) * mm]});
            skFitSpline(sketch, "E245", {"points": [v(19.17, -45.76) * mm, v(18.63, -46.73) * mm, v(17.91, -47.53) * mm, v(17.02, -48.15) * mm]});
            skFitSpline(sketch, "E246", {"points": [v(17.02, -48.15) * mm, v(16.16, -48.77) * mm, v(15.17, -49.24) * mm, v(14.05, -49.55) * mm]});
            skFitSpline(sketch, "E247", {"points": [v(14.05, -49.55) * mm, v(12.92, -49.86) * mm, v(11.78, -50.01) * mm, v(10.61, -50.01) * mm]});
            skFitSpline(sketch, "E248", {"points": [v(10.61, -50.01) * mm, v(9.41, -50.01) * mm, v(8.29, -49.88) * mm, v(7.24, -49.6) * mm]});
            skFitSpline(sketch, "E249", {"points": [v(7.24, -49.6) * mm, v(6.19, -49.33) * mm, v(5.28, -48.9) * mm, v(4.5, -48.32) * mm]});
            skFitSpline(sketch, "E250", {"points": [v(4.5, -48.32) * mm, v(3.76, -47.74) * mm, v(3.16, -46.99) * mm, v(2.7, -46.05) * mm]});
            skFitSpline(sketch, "E251", {"points": [v(2.7, -46.05) * mm, v(2.27, -45.12) * mm, v(2.06, -44) * mm, v(2.06, -42.68) * mm]});
            skFitSpline(sketch, "E252", {"points": [v(2.06, -42.68) * mm, v(2.06, -40.2) * mm, v(2.85, -38.47) * mm, v(4.44, -37.5) * mm]});
            skFitSpline(sketch, "E253", {"points": [v(4.44, -37.5) * mm, v(6.03, -36.56) * mm, v(8.29, -36.1) * mm, v(11.2, -36.1) * mm]});
            skFitSpline(sketch, "E254", {"points": [v(11.2, -36.1) * mm, v(14.34, -36.1) * mm, v(16.6, -36.56) * mm, v(17.95, -37.5) * mm]});
            skFitSpline(sketch, "E255", {"points": [v(17.95, -37.5) * mm, v(19.3, -38.43) * mm, v(19.99, -40.06) * mm, v(19.99, -42.39) * mm]});
            skFitSpline(sketch, "E256", {"points": [v(16.84, -17.17) * mm, v(16.84, -18.26) * mm, v(16.7, -19.3) * mm, v(16.44, -20.32) * mm]});
            skFitSpline(sketch, "E257", {"points": [v(16.44, -20.32) * mm, v(16.2, -21.29) * mm, v(15.82, -22.16) * mm, v(15.27, -22.94) * mm]});
            skFitSpline(sketch, "E258", {"points": [v(15.27, -22.94) * mm, v(14.77, -23.68) * mm, v(14.1, -24.28) * mm, v(13.3, -24.74) * mm]});
            skFitSpline(sketch, "E259", {"points": [v(13.3, -24.74) * mm, v(12.52, -25.17) * mm, v(11.57, -25.38) * mm, v(10.44, -25.38) * mm]});
            skFitSpline(sketch, "E260", {"points": [v(10.44, -25.38) * mm, v(8.19, -25.38) * mm, v(6.52, -24.69) * mm, v(5.43, -23.29) * mm]});
            skFitSpline(sketch, "E261", {"points": [v(5.43, -23.29) * mm, v(4.38, -21.85) * mm, v(3.86, -19.91) * mm, v(3.86, -17.47) * mm]});
            skFitSpline(sketch, "E262", {"points": [v(3.86, -17.47) * mm, v(3.86, -15.1) * mm, v(4.44, -13.22) * mm, v(5.6, -11.82) * mm]});
            skFitSpline(sketch, "E263", {"points": [v(5.6, -11.82) * mm, v(6.77, -10.38) * mm, v(8.4, -9.66) * mm, v(10.5, -9.66) * mm]});
            skFitSpline(sketch, "E264", {"points": [v(10.5, -9.66) * mm, v(12.4, -9.66) * mm, v(13.93, -10.3) * mm, v(15.1, -11.59) * mm]});
            skFitSpline(sketch, "E265", {"points": [v(15.1, -11.59) * mm, v(16.26, -12.87) * mm, v(16.84, -14.73) * mm, v(16.84, -17.17) * mm]});
            skFitSpline(sketch, "E266", {"points": [v(-0.68, -17.47) * mm, v(-0.68, -19.6) * mm, v(-0.18, -21.39) * mm, v(0.83, -22.82) * mm]});
            skFitSpline(sketch, "E267", {"points": [v(0.83, -22.82) * mm, v(1.84, -24.22) * mm, v(3.24, -25.3) * mm, v(5.02, -26.08) * mm]});
            skFitSpline(sketch, "E268", {"points": [v(5.02, -26.2) * mm, v(4.56, -26.28) * mm, v(4.07, -26.45) * mm, v(3.57, -26.72) * mm]});
            skFitSpline(sketch, "E269", {"points": [v(3.57, -26.72) * mm, v(3.06, -27) * mm, v(2.62, -27.34) * mm, v(2.23, -27.77) * mm]});
            skFitSpline(sketch, "E270", {"points": [v(2.23, -27.77) * mm, v(1.84, -28.2) * mm, v(1.51, -28.68) * mm, v(1.24, -29.23) * mm]});
            skFitSpline(sketch, "E271", {"points": [v(1.24, -29.23) * mm, v(1, -29.77) * mm, v(0.9, -30.37) * mm, v(0.9, -31.03) * mm]});
            skFitSpline(sketch, "E272", {"points": [v(0.9, -31.03) * mm, v(0.9, -32.16) * mm, v(1.2, -33.13) * mm, v(1.82, -33.94) * mm]});
            skFitSpline(sketch, "E273", {"points": [v(1.82, -33.94) * mm, v(2.44, -34.76) * mm, v(3.36, -35.34) * mm, v(4.56, -35.7) * mm]});
            skFitSpline(sketch, "E274", {"points": [v(4.56, -35.8) * mm, v(3.78, -36) * mm, v(3.03, -36.3) * mm, v(2.29, -36.68) * mm]});
            skFitSpline(sketch, "E275", {"points": [v(2.29, -36.68) * mm, v(1.55, -37.07) * mm, v(0.9, -37.6) * mm, v(0.3, -38.25) * mm]});
            skFitSpline(sketch, "E276", {"points": [v(0.3, -38.25) * mm, v(-0.27, -38.91) * mm, v(-0.76, -39.67) * mm, v(-1.15, -40.52) * mm]});
            skFitSpline(sketch, "E277", {"points": [v(-1.15, -40.52) * mm, v(-1.5, -41.38) * mm, v(-1.67, -42.3) * mm, v(-1.67, -43.32) * mm]});
            skFitSpline(sketch, "E278", {"points": [v(-1.67, -43.32) * mm, v(-1.67, -45.92) * mm, v(-0.58, -47.96) * mm, v(1.59, -49.43) * mm]});
            skFitSpline(sketch, "E279", {"points": [v(1.59, -49.43) * mm, v(3.76, -50.94) * mm, v(6.73, -51.7) * mm, v(10.5, -51.7) * mm]});
            skFitSpline(sketch, "E280", {"points": [v(10.5, -51.7) * mm, v(12.94, -51.7) * mm, v(15.04, -51.33) * mm, v(16.79, -50.6) * mm]});
            skFitSpline(sketch, "E281", {"points": [v(16.79, -50.6) * mm, v(18.53, -49.86) * mm, v(19.95, -48.93) * mm, v(21.04, -47.8) * mm]});
            skFitSpline(sketch, "E282", {"points": [v(21.04, -47.8) * mm, v(22.16, -46.68) * mm, v(22.98, -45.41) * mm, v(23.48, -44.02) * mm]});
            skFitSpline(sketch, "E283", {"points": [v(23.48, -44.02) * mm, v(24.03, -42.62) * mm, v(24.3, -41.24) * mm, v(24.3, -39.88) * mm]});
            skFitSpline(sketch, "E284", {"points": [v(24.3, -39.88) * mm, v(24.3, -38.87) * mm, v(24.1, -37.94) * mm, v(23.71, -37.09) * mm]});
            skFitSpline(sketch, "E285", {"points": [v(23.71, -37.09) * mm, v(23.37, -36.23) * mm, v(22.78, -35.48) * mm, v(21.97, -34.82) * mm]});
            skFitSpline(sketch, "E286", {"points": [v(21.97, -34.82) * mm, v(21.2, -34.16) * mm, v(20.16, -33.63) * mm, v(18.88, -33.24) * mm]});
            skFitSpline(sketch, "E287", {"points": [v(18.88, -33.24) * mm, v(17.64, -32.86) * mm, v(16.13, -32.64) * mm, v(14.34, -32.6) * mm]});
            skFitSpline(sketch, "E288", {"points": [v(14.34, -32.6) * mm, v(13.25, -32.57) * mm, v(12.19, -32.55) * mm, v(11.14, -32.55) * mm]});
            skFitSpline(sketch, "E289", {"points": [v(11.14, -32.55) * mm, v(10.1, -32.5) * mm, v(9.02, -32.47) * mm, v(7.94, -32.43) * mm]});
            skFitSpline(sketch, "E290", {"points": [v(7.94, -32.43) * mm, v(6.62, -32.4) * mm, v(5.7, -32.14) * mm, v(5.2, -31.67) * mm]});
            skFitSpline(sketch, "E291", {"points": [v(5.2, -31.67) * mm, v(4.73, -31.2) * mm, v(4.5, -30.47) * mm, v(4.5, -29.46) * mm]});
            skFitSpline(sketch, "E292", {"points": [v(4.5, -29.46) * mm, v(4.5, -28.68) * mm, v(4.8, -28.04) * mm, v(5.37, -27.54) * mm]});
            skFitSpline(sketch, "E293", {"points": [v(5.37, -27.54) * mm, v(6, -27.03) * mm, v(6.65, -26.78) * mm, v(7.35, -26.78) * mm]});
            skFitSpline(sketch, "E294", {"points": [v(7.35, -26.78) * mm, v(7.9, -26.78) * mm, v(8.42, -26.8) * mm, v(8.93, -26.84) * mm]});
            skFitSpline(sketch, "E295", {"points": [v(8.93, -26.84) * mm, v(9.47, -26.88) * mm, v(10.01, -26.9) * mm, v(10.56, -26.9) * mm]});
            skFitSpline(sketch, "E296", {"points": [v(10.56, -26.9) * mm, v(13.86, -26.9) * mm, v(16.48, -26.08) * mm, v(18.42, -24.45) * mm]});
            skFitSpline(sketch, "E297", {"points": [v(18.42, -24.45) * mm, v(20.4, -22.78) * mm, v(21.39, -20.5) * mm, v(21.39, -17.58) * mm]});
            skFitSpline(sketch, "E298", {"points": [v(21.39, -17.58) * mm, v(21.39, -16.1) * mm, v(21.02, -14.7) * mm, v(20.28, -13.33) * mm]});
            skFitSpline(sketch, "E299", {"points": [v(20.28, -13.33) * mm, v(19.54, -11.93) * mm, v(18.57, -10.9) * mm, v(17.37, -10.25) * mm]});
            skFitSpline(sketch, "E300", {"points": [v(17.48, -10.13) * mm, v(18.53, -10.17) * mm, v(19.58, -10.25) * mm, v(20.63, -10.36) * mm]});
            skFitSpline(sketch, "E301", {"points": [v(20.63, -10.36) * mm, v(21.72, -10.44) * mm, v(22.82, -10.52) * mm, v(23.95, -10.6) * mm]});
            skFitSpline(sketch, "E302", {"points": [v(23.95, -10.6) * mm, v(23.9, -10.4) * mm, v(23.87, -10.2) * mm, v(23.83, -10.01) * mm]});
            skFitSpline(sketch, "E303", {"points": [v(23.83, -10.01) * mm, v(23.83, -9.78) * mm, v(23.83, -9.57) * mm, v(23.83, -9.37) * mm]});
            skFitSpline(sketch, "E304", {"points": [v(23.83, -9.37) * mm, v(23.83, -9.18) * mm, v(23.83, -8.98) * mm, v(23.83, -8.8) * mm]});
            skFitSpline(sketch, "E305", {"points": [v(23.83, -8.8) * mm, v(23.87, -8.56) * mm, v(23.9, -8.34) * mm, v(23.95, -8.15) * mm]});
            skFitSpline(sketch, "E306", {"points": [v(23.95, -8.15) * mm, v(22.98, -8.34) * mm, v(21.4, -8.44) * mm, v(19.23, -8.44) * mm]});
            skFitSpline(sketch, "E307", {"points": [v(19.23, -8.44) * mm, v(18.8, -8.44) * mm, v(18.24, -8.42) * mm, v(17.54, -8.38) * mm]});
            skFitSpline(sketch, "E308", {"points": [v(17.54, -8.38) * mm, v(16.84, -8.34) * mm, v(16.05, -8.29) * mm, v(15.16, -8.2) * mm]});
            skFitSpline(sketch, "E309", {"points": [v(15.16, -8.2) * mm, v(14.1, -8.13) * mm, v(13.23, -8.07) * mm, v(12.54, -8.03) * mm]});
            skFitSpline(sketch, "E310", {"points": [v(12.54, -8.03) * mm, v(11.88, -8) * mm, v(11.18, -7.98) * mm, v(10.44, -7.98) * mm]});
            skFitSpline(sketch, "E311", {"points": [v(10.44, -7.98) * mm, v(8.93, -7.98) * mm, v(7.49, -8.17) * mm, v(6.13, -8.56) * mm]});
            skFitSpline(sketch, "E312", {"points": [v(6.13, -8.56) * mm, v(4.81, -8.95) * mm, v(3.63, -9.53) * mm, v(2.58, -10.3) * mm]});
            skFitSpline(sketch, "E313", {"points": [v(2.58, -10.3) * mm, v(1.57, -11.08) * mm, v(0.77, -12.07) * mm, v(0.2, -13.27) * mm]});
            skFitSpline(sketch, "E314", {"points": [v(0.2, -13.27) * mm, v(-0.4, -14.44) * mm, v(-0.68, -15.84) * mm, v(-0.68, -17.47) * mm]});
            skSolve(sketch);
        }
        {
            var Q0;
            Q0=makeQuery(id+"F0.imprint","IMPRINT",FACE,{"disambiguationData":[TD([[makeQuery(id+"F0.imprint","IMPRINT",EDGE,{"derivedFrom":sQuery(id+"F0.wireOp",EDGE,"E23")}),1.0]])]});
            var Q1;
            Q1=makeQuery(id+"F0.imprint","IMPRINT",FACE,{"disambiguationData":[TD([[makeQuery(id+"F0.imprint","IMPRINT",EDGE,{"derivedFrom":sQuery(id+"F0.wireOp",EDGE,"E53")}),1.0]])]});
            var Q2;
            Q2=makeQuery(id+"F0.imprint","IMPRINT",FACE,{"disambiguationData":[TD([[makeQuery(id+"F0.imprint","IMPRINT",EDGE,{"derivedFrom":sQuery(id+"F0.wireOp",EDGE,"E1")}),-1.0]])]});
            var Q3;
            Q3=makeQuery(id+"F0.imprint","IMPRINT",FACE,{"disambiguationData":[TD([[makeQuery(id+"F0.imprint","IMPRINT",EDGE,{"derivedFrom":sQuery(id+"F0.wireOp",EDGE,"E7")}),-1.0]])]});
            var Q4;
            Q4=makeQuery(id+"F0.imprint","IMPRINT",FACE,{"disambiguationData":[TD([[makeQuery(id+"F0.imprint","IMPRINT",EDGE,{"derivedFrom":sQuery(id+"F0.wireOp",EDGE,"E14")}),-1.0]])]});
            var Q5;
            Q5=makeQuery(id+"F0.imprint","IMPRINT",FACE,{"disambiguationData":[TD([[makeQuery(id+"F0.imprint","IMPRINT",EDGE,{"derivedFrom":sQuery(id+"F0.wireOp",EDGE,"E18")}),-1.0]])]});
            extrude(context, id + "F1", {"entities" : qUnion([Q0, Q1, Q2, Q3, Q4, Q5]), "depth" : 2 * mm, "offsetDistance" : 25 * mm});
        }
    });
